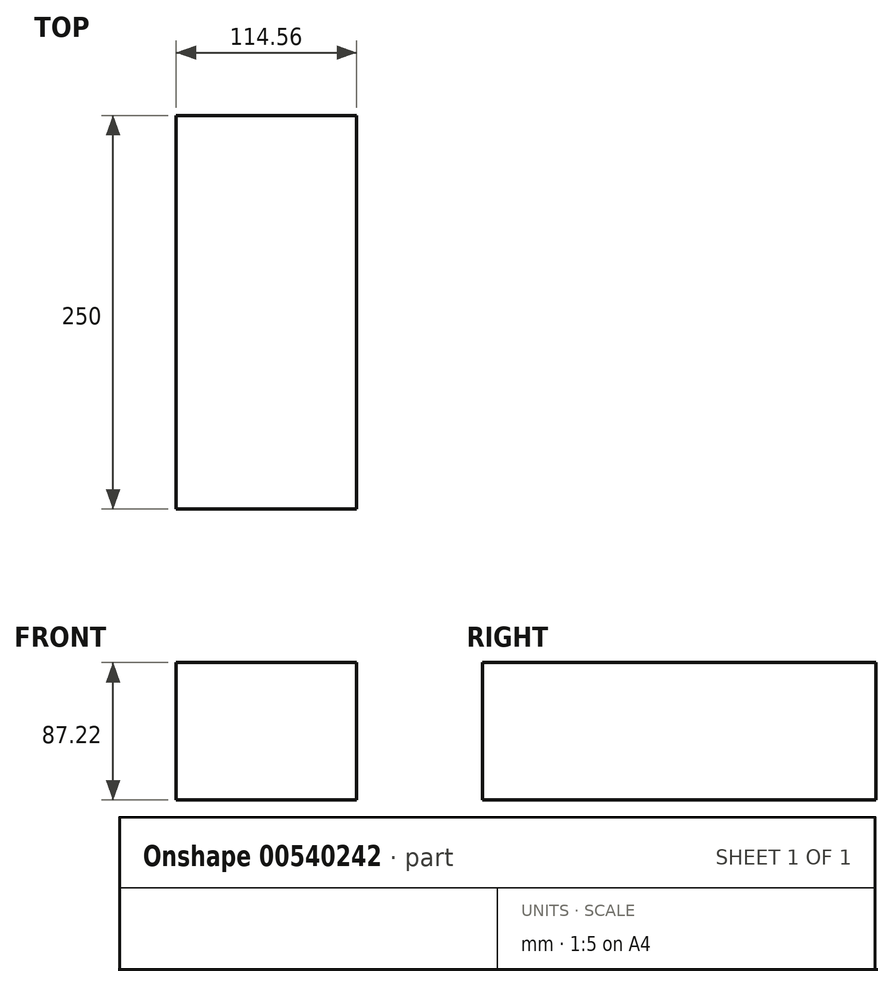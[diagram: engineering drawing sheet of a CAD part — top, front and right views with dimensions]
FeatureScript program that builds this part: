
annotation { "Feature Type Name" : "Feature", "Feature Type Description" : "" }
export const myFeature = defineFeature(function(context is Context, id is Id, definition is map)
    precondition{}
    {
        {
            var Q0;
            Q0=qCreatedBy(makeId("Front.planeOp"),FACE);
            var sketch = newSketch(context, id + "F0", { "sketchPlane" : qUnion([Q0])});
            skLineSegment(sketch, "E0.bottom", {"start": v(57.28, 43.6) * mm, "end": v(-57.28, 43.6) * mm});
            skLineSegment(sketch, "E0.top", {"start": v(57.28, -43.6) * mm, "end": v(-57.28, -43.6) * mm});
            skLineSegment(sketch, "E0.left", {"start": v(57.28, 43.6) * mm, "end": v(57.28, -43.6) * mm});
            skLineSegment(sketch, "E0.right", {"start": v(-57.28, 43.6) * mm, "end": v(-57.28, -43.6) * mm});
            skPoint(sketch, "E0.middle", {"position": v(0, 0) * mm});
            skSolve(sketch);
        }
        {
            var Q0;
            Q0 = qSketchRegion(id + "F0", true);
            extrude(context, id + "F1", {"entities" : qUnion([Q0]), "endBound" : BoundingType.SYMMETRIC, "depth" : 250 * mm, "offsetDistance" : 25 * mm});
        }
    });
